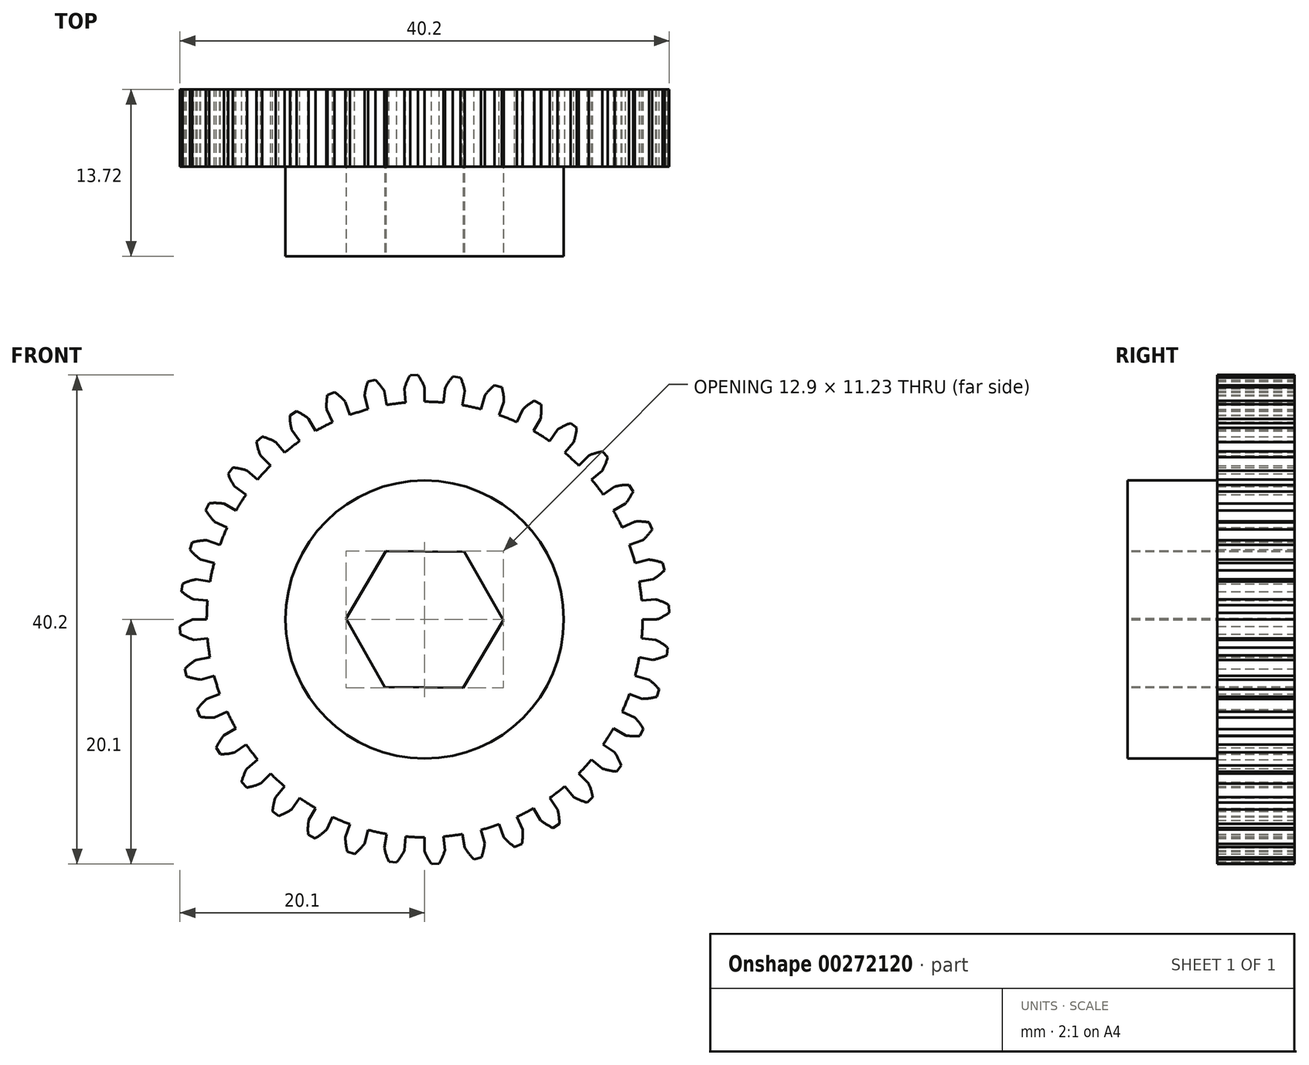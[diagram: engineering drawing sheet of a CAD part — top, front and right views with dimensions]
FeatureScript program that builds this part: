
annotation { "Feature Type Name" : "Feature", "Feature Type Description" : "" }
export const myFeature = defineFeature(function(context is Context, id is Id, definition is map)
    precondition{}
    {
        {
            var Q0;
            Q0=qCreatedBy(makeId("Front.planeOp"),FACE);
            var sketch = newSketch(context, id + "F0", { "sketchPlane" : qUnion([Q0])});
            skArc(sketch, "E0", {"start": v(-4.45, 17.34) * mm, "mid": v(-5.38, 17.07) * mm, "end": v(-6.3, 16.75) * mm});
            skLineSegment(sketch, "E1.trimOffspring", {"start": v(0, 23.81) * mm, "end": v(0, 30.83) * mm});
            skArc(sketch, "E2.trimOffspring", {"start": v(0, 19.05) * mm, "mid": v(-0.25, 19.6) * mm, "end": v(-0.56, 20.1) * mm});
            skArc(sketch, "E3.MirrorCS", {"start": v(-1.66, 18.98) * mm, "mid": v(-1.46, 19.54) * mm, "end": v(-1.2, 20.07) * mm});
            skLineSegment(sketch, "E4.trimOffspring", {"start": v(-1.56, 17.83) * mm, "end": v(-1.66, 18.98) * mm});
            skLineSegment(sketch, "E5.trimOffspring", {"start": v(0, 17.9) * mm, "end": v(0, 19.05) * mm});
            skArc(sketch, "E6.trimOffspring", {"start": v(0, 17.9) * mm, "mid": v(-0.1, 17.9) * mm, "end": v(-0.2, 17.9) * mm});
            skArc(sketch, "E7", {"start": v(-1.56, 17.84) * mm, "mid": v(-2.34, 17.75) * mm, "end": v(-3.1, 17.63) * mm});
            skLineSegment(sketch, "E8", {"start": v(-1.2, 20.07) * mm, "end": v(-0.56, 20.1) * mm});
            skLineSegment(sketch, "E9.1.0", {"start": v(-4.63, 17.3) * mm, "end": v(-4.93, 18.4) * mm});
            skArc(sketch, "E9.1.1", {"start": v(-4.93, 18.4) * mm, "mid": v(-4.83, 18.99) * mm, "end": v(-4.66, 19.56) * mm});
            skLineSegment(sketch, "E9.1.2", {"start": v(-4.66, 19.56) * mm, "end": v(-4.04, 19.7) * mm});
            skArc(sketch, "E9.1.3", {"start": v(-3.3, 18.76) * mm, "mid": v(-3.65, 19.25) * mm, "end": v(-4.04, 19.7) * mm});
            skLineSegment(sketch, "E9.1.4", {"start": v(-3.1, 17.63) * mm, "end": v(-3.3, 18.76) * mm});
            skLineSegment(sketch, "E9.2.0", {"start": v(-7.57, 16.22) * mm, "end": v(-8.05, 17.27) * mm});
            skArc(sketch, "E9.2.1", {"start": v(-8.05, 17.27) * mm, "mid": v(-8.05, 17.86) * mm, "end": v(-7.98, 18.45) * mm});
            skLineSegment(sketch, "E9.2.2", {"start": v(-7.98, 18.45) * mm, "end": v(-7.4, 18.7) * mm});
            skArc(sketch, "E9.2.3", {"start": v(-6.52, 17.9) * mm, "mid": v(-6.93, 18.32) * mm, "end": v(-7.4, 18.7) * mm});
            skLineSegment(sketch, "E9.2.4", {"start": v(-6.12, 16.82) * mm, "end": v(-6.52, 17.9) * mm});
            skLineSegment(sketch, "E9.3.0", {"start": v(-10.27, 14.66) * mm, "end": v(-10.93, 15.6) * mm});
            skArc(sketch, "E9.3.1", {"start": v(-10.93, 15.6) * mm, "mid": v(-11.03, 16.19) * mm, "end": v(-11.07, 16.78) * mm});
            skLineSegment(sketch, "E9.3.2", {"start": v(-11.07, 16.78) * mm, "end": v(-10.53, 17.12) * mm});
            skArc(sketch, "E9.3.3", {"start": v(-9.52, 16.5) * mm, "mid": v(-10, 16.84) * mm, "end": v(-10.53, 17.12) * mm});
            skLineSegment(sketch, "E9.3.4", {"start": v(-8.95, 15.5) * mm, "end": v(-9.53, 16.5) * mm});
            skLineSegment(sketch, "E9.4.0", {"start": v(-12.66, 12.66) * mm, "end": v(-13.47, 13.47) * mm});
            skArc(sketch, "E9.4.1", {"start": v(-13.47, 13.47) * mm, "mid": v(-13.68, 14.03) * mm, "end": v(-13.81, 14.6) * mm});
            skLineSegment(sketch, "E9.4.2", {"start": v(-13.81, 14.6) * mm, "end": v(-13.35, 15.03) * mm});
            skArc(sketch, "E9.4.3", {"start": v(-12.25, 14.6) * mm, "mid": v(-12.78, 14.85) * mm, "end": v(-13.35, 15.03) * mm});
            skLineSegment(sketch, "E9.4.4", {"start": v(-11.5, 13.71) * mm, "end": v(-12.25, 14.6) * mm});
            skLineSegment(sketch, "E9.5.0", {"start": v(-14.66, 10.27) * mm, "end": v(-15.6, 10.93) * mm});
            skArc(sketch, "E9.5.1", {"start": v(-15.6, 10.93) * mm, "mid": v(-15.9, 11.44) * mm, "end": v(-16.14, 11.99) * mm});
            skLineSegment(sketch, "E9.5.2", {"start": v(-16.14, 11.99) * mm, "end": v(-15.76, 12.49) * mm});
            skArc(sketch, "E9.5.3", {"start": v(-14.6, 12.25) * mm, "mid": v(-15.17, 12.4) * mm, "end": v(-15.76, 12.49) * mm});
            skLineSegment(sketch, "E9.5.4", {"start": v(-13.71, 11.5) * mm, "end": v(-14.6, 12.25) * mm});
            skLineSegment(sketch, "E9.6.0", {"start": v(-16.22, 7.57) * mm, "end": v(-17.27, 8.05) * mm});
            skArc(sketch, "E9.6.1", {"start": v(-17.27, 8.05) * mm, "mid": v(-17.65, 8.5) * mm, "end": v(-17.98, 9) * mm});
            skLineSegment(sketch, "E9.6.2", {"start": v(-17.98, 9) * mm, "end": v(-17.68, 9.56) * mm});
            skArc(sketch, "E9.6.3", {"start": v(-16.5, 9.53) * mm, "mid": v(-17.09, 9.58) * mm, "end": v(-17.68, 9.56) * mm});
            skLineSegment(sketch, "E9.6.4", {"start": v(-15.5, 8.95) * mm, "end": v(-16.5, 9.53) * mm});
            skLineSegment(sketch, "E9.7.0", {"start": v(-17.3, 4.63) * mm, "end": v(-18.4, 4.93) * mm});
            skArc(sketch, "E9.7.1", {"start": v(-18.4, 4.93) * mm, "mid": v(-18.86, 5.3) * mm, "end": v(-19.27, 5.74) * mm});
            skLineSegment(sketch, "E9.7.2", {"start": v(-19.27, 5.74) * mm, "end": v(-19.08, 6.35) * mm});
            skArc(sketch, "E9.7.3", {"start": v(-17.9, 6.52) * mm, "mid": v(-18.5, 6.47) * mm, "end": v(-19.08, 6.35) * mm});
            skLineSegment(sketch, "E9.7.4", {"start": v(-16.82, 6.12) * mm, "end": v(-17.9, 6.52) * mm});
            skLineSegment(sketch, "E9.8.0", {"start": v(-17.83, 1.56) * mm, "end": v(-18.98, 1.66) * mm});
            skArc(sketch, "E9.8.1", {"start": v(-18.98, 1.66) * mm, "mid": v(-19.5, 1.95) * mm, "end": v(-19.97, 2.31) * mm});
            skLineSegment(sketch, "E9.8.2", {"start": v(-19.97, 2.31) * mm, "end": v(-19.89, 2.94) * mm});
            skArc(sketch, "E9.8.3", {"start": v(-18.76, 3.3) * mm, "mid": v(-19.34, 3.16) * mm, "end": v(-19.89, 2.94) * mm});
            skLineSegment(sketch, "E9.8.4", {"start": v(-17.63, 3.1) * mm, "end": v(-18.76, 3.3) * mm});
            skLineSegment(sketch, "E9.9.0", {"start": v(-17.83, -1.56) * mm, "end": v(-18.98, -1.66) * mm});
            skArc(sketch, "E9.9.1", {"start": v(-18.98, -1.66) * mm, "mid": v(-19.54, -1.46) * mm, "end": v(-20.07, -1.2) * mm});
            skLineSegment(sketch, "E9.9.2", {"start": v(-20.07, -1.2) * mm, "end": v(-20.1, -0.56) * mm});
            skArc(sketch, "E9.9.3", {"start": v(-19.05, 0) * mm, "mid": v(-19.6, -0.25) * mm, "end": v(-20.1, -0.56) * mm});
            skLineSegment(sketch, "E9.9.4", {"start": v(-17.9, 0) * mm, "end": v(-19.05, 0) * mm});
            skLineSegment(sketch, "E9.10.0", {"start": v(-17.3, -4.63) * mm, "end": v(-18.4, -4.93) * mm});
            skArc(sketch, "E9.10.1", {"start": v(-18.4, -4.93) * mm, "mid": v(-18.99, -4.83) * mm, "end": v(-19.56, -4.66) * mm});
            skLineSegment(sketch, "E9.10.2", {"start": v(-19.56, -4.66) * mm, "end": v(-19.7, -4.04) * mm});
            skArc(sketch, "E9.10.3", {"start": v(-18.76, -3.3) * mm, "mid": v(-19.25, -3.65) * mm, "end": v(-19.7, -4.04) * mm});
            skLineSegment(sketch, "E9.10.4", {"start": v(-17.63, -3.1) * mm, "end": v(-18.76, -3.3) * mm});
            skLineSegment(sketch, "E9.11.0", {"start": v(-16.22, -7.57) * mm, "end": v(-17.27, -8.05) * mm});
            skArc(sketch, "E9.11.1", {"start": v(-17.27, -8.05) * mm, "mid": v(-17.86, -8.05) * mm, "end": v(-18.45, -7.98) * mm});
            skLineSegment(sketch, "E9.11.2", {"start": v(-18.45, -7.98) * mm, "end": v(-18.7, -7.4) * mm});
            skArc(sketch, "E9.11.3", {"start": v(-17.9, -6.52) * mm, "mid": v(-18.32, -6.93) * mm, "end": v(-18.7, -7.4) * mm});
            skLineSegment(sketch, "E9.11.4", {"start": v(-16.82, -6.12) * mm, "end": v(-17.9, -6.52) * mm});
            skLineSegment(sketch, "E9.12.0", {"start": v(-14.66, -10.27) * mm, "end": v(-15.6, -10.93) * mm});
            skArc(sketch, "E9.12.1", {"start": v(-15.6, -10.93) * mm, "mid": v(-16.19, -11.03) * mm, "end": v(-16.78, -11.07) * mm});
            skLineSegment(sketch, "E9.12.2", {"start": v(-16.78, -11.07) * mm, "end": v(-17.12, -10.53) * mm});
            skArc(sketch, "E9.12.3", {"start": v(-16.5, -9.52) * mm, "mid": v(-16.84, -10) * mm, "end": v(-17.12, -10.53) * mm});
            skLineSegment(sketch, "E9.12.4", {"start": v(-15.5, -8.95) * mm, "end": v(-16.5, -9.52) * mm});
            skLineSegment(sketch, "E9.13.0", {"start": v(-12.66, -12.66) * mm, "end": v(-13.47, -13.47) * mm});
            skArc(sketch, "E9.13.1", {"start": v(-13.47, -13.47) * mm, "mid": v(-14.03, -13.68) * mm, "end": v(-14.6, -13.81) * mm});
            skLineSegment(sketch, "E9.13.2", {"start": v(-14.6, -13.81) * mm, "end": v(-15.03, -13.35) * mm});
            skArc(sketch, "E9.13.3", {"start": v(-14.6, -12.25) * mm, "mid": v(-14.85, -12.78) * mm, "end": v(-15.03, -13.35) * mm});
            skLineSegment(sketch, "E9.13.4", {"start": v(-13.71, -11.5) * mm, "end": v(-14.6, -12.25) * mm});
            skLineSegment(sketch, "E9.14.0", {"start": v(-10.27, -14.66) * mm, "end": v(-10.93, -15.6) * mm});
            skArc(sketch, "E9.14.1", {"start": v(-10.93, -15.6) * mm, "mid": v(-11.44, -15.9) * mm, "end": v(-11.99, -16.14) * mm});
            skLineSegment(sketch, "E9.14.2", {"start": v(-11.99, -16.14) * mm, "end": v(-12.49, -15.76) * mm});
            skArc(sketch, "E9.14.3", {"start": v(-12.25, -14.6) * mm, "mid": v(-12.4, -15.17) * mm, "end": v(-12.49, -15.76) * mm});
            skLineSegment(sketch, "E9.14.4", {"start": v(-11.5, -13.71) * mm, "end": v(-12.25, -14.6) * mm});
            skLineSegment(sketch, "E9.15.0", {"start": v(-7.57, -16.22) * mm, "end": v(-8.05, -17.27) * mm});
            skArc(sketch, "E9.15.1", {"start": v(-8.05, -17.27) * mm, "mid": v(-8.5, -17.65) * mm, "end": v(-9, -17.98) * mm});
            skLineSegment(sketch, "E9.15.2", {"start": v(-9, -17.98) * mm, "end": v(-9.56, -17.68) * mm});
            skArc(sketch, "E9.15.3", {"start": v(-9.53, -16.5) * mm, "mid": v(-9.58, -17.09) * mm, "end": v(-9.56, -17.68) * mm});
            skLineSegment(sketch, "E9.15.4", {"start": v(-8.95, -15.5) * mm, "end": v(-9.53, -16.5) * mm});
            skLineSegment(sketch, "E9.16.0", {"start": v(-4.63, -17.3) * mm, "end": v(-4.93, -18.4) * mm});
            skArc(sketch, "E9.16.1", {"start": v(-4.93, -18.4) * mm, "mid": v(-5.3, -18.86) * mm, "end": v(-5.74, -19.27) * mm});
            skLineSegment(sketch, "E9.16.2", {"start": v(-5.74, -19.27) * mm, "end": v(-6.35, -19.08) * mm});
            skArc(sketch, "E9.16.3", {"start": v(-6.52, -17.9) * mm, "mid": v(-6.47, -18.5) * mm, "end": v(-6.35, -19.08) * mm});
            skLineSegment(sketch, "E9.16.4", {"start": v(-6.12, -16.82) * mm, "end": v(-6.52, -17.9) * mm});
            skLineSegment(sketch, "E9.17.0", {"start": v(-1.56, -17.83) * mm, "end": v(-1.66, -18.98) * mm});
            skArc(sketch, "E9.17.1", {"start": v(-1.66, -18.98) * mm, "mid": v(-1.95, -19.5) * mm, "end": v(-2.31, -19.97) * mm});
            skLineSegment(sketch, "E9.17.2", {"start": v(-2.31, -19.97) * mm, "end": v(-2.94, -19.89) * mm});
            skArc(sketch, "E9.17.3", {"start": v(-3.3, -18.76) * mm, "mid": v(-3.16, -19.34) * mm, "end": v(-2.94, -19.89) * mm});
            skLineSegment(sketch, "E9.17.4", {"start": v(-3.1, -17.63) * mm, "end": v(-3.3, -18.76) * mm});
            skLineSegment(sketch, "E9.18.0", {"start": v(1.56, -17.83) * mm, "end": v(1.66, -18.98) * mm});
            skArc(sketch, "E9.18.1", {"start": v(1.66, -18.98) * mm, "mid": v(1.46, -19.54) * mm, "end": v(1.2, -20.07) * mm});
            skLineSegment(sketch, "E9.18.2", {"start": v(1.2, -20.07) * mm, "end": v(0.56, -20.1) * mm});
            skArc(sketch, "E9.18.3", {"start": v(0, -19.05) * mm, "mid": v(0.25, -19.6) * mm, "end": v(0.56, -20.1) * mm});
            skLineSegment(sketch, "E9.18.4", {"start": v(0, -17.9) * mm, "end": v(0, -19.05) * mm});
            skLineSegment(sketch, "E9.19.0", {"start": v(4.63, -17.3) * mm, "end": v(4.93, -18.4) * mm});
            skArc(sketch, "E9.19.1", {"start": v(4.93, -18.4) * mm, "mid": v(4.83, -18.99) * mm, "end": v(4.66, -19.56) * mm});
            skLineSegment(sketch, "E9.19.2", {"start": v(4.66, -19.56) * mm, "end": v(4.04, -19.7) * mm});
            skArc(sketch, "E9.19.3", {"start": v(3.3, -18.76) * mm, "mid": v(3.65, -19.25) * mm, "end": v(4.04, -19.7) * mm});
            skLineSegment(sketch, "E9.19.4", {"start": v(3.1, -17.63) * mm, "end": v(3.3, -18.76) * mm});
            skLineSegment(sketch, "E9.20.0", {"start": v(7.57, -16.22) * mm, "end": v(8.05, -17.27) * mm});
            skArc(sketch, "E9.20.1", {"start": v(8.05, -17.27) * mm, "mid": v(8.05, -17.86) * mm, "end": v(7.98, -18.45) * mm});
            skLineSegment(sketch, "E9.20.2", {"start": v(7.98, -18.45) * mm, "end": v(7.4, -18.7) * mm});
            skArc(sketch, "E9.20.3", {"start": v(6.52, -17.9) * mm, "mid": v(6.93, -18.32) * mm, "end": v(7.4, -18.7) * mm});
            skLineSegment(sketch, "E9.20.4", {"start": v(6.12, -16.82) * mm, "end": v(6.52, -17.9) * mm});
            skLineSegment(sketch, "E9.21.0", {"start": v(10.27, -14.66) * mm, "end": v(10.93, -15.6) * mm});
            skArc(sketch, "E9.21.1", {"start": v(10.93, -15.6) * mm, "mid": v(11.03, -16.19) * mm, "end": v(11.07, -16.78) * mm});
            skLineSegment(sketch, "E9.21.2", {"start": v(11.07, -16.78) * mm, "end": v(10.53, -17.12) * mm});
            skArc(sketch, "E9.21.3", {"start": v(9.52, -16.5) * mm, "mid": v(10, -16.84) * mm, "end": v(10.53, -17.12) * mm});
            skLineSegment(sketch, "E9.21.4", {"start": v(8.95, -15.5) * mm, "end": v(9.53, -16.5) * mm});
            skLineSegment(sketch, "E9.22.0", {"start": v(12.66, -12.66) * mm, "end": v(13.47, -13.47) * mm});
            skArc(sketch, "E9.22.1", {"start": v(13.47, -13.47) * mm, "mid": v(13.68, -14.03) * mm, "end": v(13.81, -14.6) * mm});
            skLineSegment(sketch, "E9.22.2", {"start": v(13.81, -14.6) * mm, "end": v(13.35, -15.03) * mm});
            skArc(sketch, "E9.22.3", {"start": v(12.25, -14.6) * mm, "mid": v(12.78, -14.85) * mm, "end": v(13.35, -15.03) * mm});
            skLineSegment(sketch, "E9.22.4", {"start": v(11.5, -13.71) * mm, "end": v(12.25, -14.6) * mm});
            skLineSegment(sketch, "E9.23.0", {"start": v(14.66, -10.27) * mm, "end": v(15.6, -10.93) * mm});
            skArc(sketch, "E9.23.1", {"start": v(15.6, -10.93) * mm, "mid": v(15.9, -11.44) * mm, "end": v(16.14, -11.99) * mm});
            skLineSegment(sketch, "E9.23.2", {"start": v(16.14, -11.99) * mm, "end": v(15.76, -12.49) * mm});
            skArc(sketch, "E9.23.3", {"start": v(14.6, -12.25) * mm, "mid": v(15.17, -12.4) * mm, "end": v(15.76, -12.49) * mm});
            skLineSegment(sketch, "E9.23.4", {"start": v(13.71, -11.5) * mm, "end": v(14.6, -12.25) * mm});
            skLineSegment(sketch, "E9.24.0", {"start": v(16.22, -7.57) * mm, "end": v(17.27, -8.05) * mm});
            skArc(sketch, "E9.24.1", {"start": v(17.27, -8.05) * mm, "mid": v(17.65, -8.5) * mm, "end": v(17.98, -9) * mm});
            skLineSegment(sketch, "E9.24.2", {"start": v(17.98, -9) * mm, "end": v(17.68, -9.56) * mm});
            skArc(sketch, "E9.24.3", {"start": v(16.5, -9.53) * mm, "mid": v(17.09, -9.58) * mm, "end": v(17.68, -9.56) * mm});
            skLineSegment(sketch, "E9.24.4", {"start": v(15.5, -8.95) * mm, "end": v(16.5, -9.53) * mm});
            skLineSegment(sketch, "E9.25.0", {"start": v(17.3, -4.63) * mm, "end": v(18.4, -4.93) * mm});
            skArc(sketch, "E9.25.1", {"start": v(18.4, -4.93) * mm, "mid": v(18.86, -5.3) * mm, "end": v(19.27, -5.74) * mm});
            skLineSegment(sketch, "E9.25.2", {"start": v(19.27, -5.74) * mm, "end": v(19.08, -6.35) * mm});
            skArc(sketch, "E9.25.3", {"start": v(17.9, -6.52) * mm, "mid": v(18.5, -6.47) * mm, "end": v(19.08, -6.35) * mm});
            skLineSegment(sketch, "E9.25.4", {"start": v(16.82, -6.12) * mm, "end": v(17.9, -6.52) * mm});
            skLineSegment(sketch, "E9.26.0", {"start": v(17.83, -1.56) * mm, "end": v(18.98, -1.66) * mm});
            skArc(sketch, "E9.26.1", {"start": v(18.98, -1.66) * mm, "mid": v(19.5, -1.95) * mm, "end": v(19.97, -2.31) * mm});
            skLineSegment(sketch, "E9.26.2", {"start": v(19.97, -2.31) * mm, "end": v(19.89, -2.94) * mm});
            skArc(sketch, "E9.26.3", {"start": v(18.76, -3.3) * mm, "mid": v(19.34, -3.16) * mm, "end": v(19.89, -2.94) * mm});
            skLineSegment(sketch, "E9.26.4", {"start": v(17.63, -3.1) * mm, "end": v(18.76, -3.3) * mm});
            skLineSegment(sketch, "E9.27.0", {"start": v(17.83, 1.56) * mm, "end": v(18.98, 1.66) * mm});
            skArc(sketch, "E9.27.1", {"start": v(18.98, 1.66) * mm, "mid": v(19.54, 1.46) * mm, "end": v(20.07, 1.2) * mm});
            skLineSegment(sketch, "E9.27.2", {"start": v(20.07, 1.2) * mm, "end": v(20.1, 0.56) * mm});
            skArc(sketch, "E9.27.3", {"start": v(19.05, 0) * mm, "mid": v(19.6, 0.25) * mm, "end": v(20.1, 0.56) * mm});
            skLineSegment(sketch, "E9.27.4", {"start": v(17.9, 0) * mm, "end": v(19.05, 0) * mm});
            skLineSegment(sketch, "E9.28.0", {"start": v(17.3, 4.63) * mm, "end": v(18.4, 4.93) * mm});
            skArc(sketch, "E9.28.1", {"start": v(18.4, 4.93) * mm, "mid": v(18.99, 4.83) * mm, "end": v(19.56, 4.66) * mm});
            skLineSegment(sketch, "E9.28.2", {"start": v(19.56, 4.66) * mm, "end": v(19.7, 4.04) * mm});
            skArc(sketch, "E9.28.3", {"start": v(18.76, 3.3) * mm, "mid": v(19.25, 3.65) * mm, "end": v(19.7, 4.04) * mm});
            skLineSegment(sketch, "E9.28.4", {"start": v(17.63, 3.1) * mm, "end": v(18.76, 3.3) * mm});
            skLineSegment(sketch, "E9.29.0", {"start": v(16.22, 7.57) * mm, "end": v(17.27, 8.05) * mm});
            skArc(sketch, "E9.29.1", {"start": v(17.27, 8.05) * mm, "mid": v(17.86, 8.05) * mm, "end": v(18.45, 7.98) * mm});
            skLineSegment(sketch, "E9.29.2", {"start": v(18.45, 7.98) * mm, "end": v(18.7, 7.4) * mm});
            skArc(sketch, "E9.29.3", {"start": v(17.9, 6.52) * mm, "mid": v(18.32, 6.93) * mm, "end": v(18.7, 7.4) * mm});
            skLineSegment(sketch, "E9.29.4", {"start": v(16.82, 6.12) * mm, "end": v(17.9, 6.52) * mm});
            skLineSegment(sketch, "E9.30.0", {"start": v(14.66, 10.27) * mm, "end": v(15.6, 10.93) * mm});
            skArc(sketch, "E9.30.1", {"start": v(15.6, 10.93) * mm, "mid": v(16.19, 11.03) * mm, "end": v(16.78, 11.07) * mm});
            skLineSegment(sketch, "E9.30.2", {"start": v(16.78, 11.07) * mm, "end": v(17.12, 10.53) * mm});
            skArc(sketch, "E9.30.3", {"start": v(16.5, 9.52) * mm, "mid": v(16.84, 10) * mm, "end": v(17.12, 10.53) * mm});
            skLineSegment(sketch, "E9.30.4", {"start": v(15.5, 8.95) * mm, "end": v(16.5, 9.52) * mm});
            skLineSegment(sketch, "E9.31.0", {"start": v(12.66, 12.66) * mm, "end": v(13.47, 13.47) * mm});
            skArc(sketch, "E9.31.1", {"start": v(13.47, 13.47) * mm, "mid": v(14.03, 13.68) * mm, "end": v(14.6, 13.81) * mm});
            skLineSegment(sketch, "E9.31.2", {"start": v(14.6, 13.81) * mm, "end": v(15.03, 13.35) * mm});
            skArc(sketch, "E9.31.3", {"start": v(14.6, 12.25) * mm, "mid": v(14.85, 12.78) * mm, "end": v(15.03, 13.35) * mm});
            skLineSegment(sketch, "E9.31.4", {"start": v(13.71, 11.5) * mm, "end": v(14.6, 12.25) * mm});
            skLineSegment(sketch, "E9.32.0", {"start": v(10.27, 14.66) * mm, "end": v(10.93, 15.6) * mm});
            skArc(sketch, "E9.32.1", {"start": v(10.93, 15.6) * mm, "mid": v(11.44, 15.9) * mm, "end": v(11.99, 16.14) * mm});
            skLineSegment(sketch, "E9.32.2", {"start": v(11.99, 16.14) * mm, "end": v(12.49, 15.76) * mm});
            skArc(sketch, "E9.32.3", {"start": v(12.25, 14.6) * mm, "mid": v(12.4, 15.17) * mm, "end": v(12.49, 15.76) * mm});
            skLineSegment(sketch, "E9.32.4", {"start": v(11.5, 13.71) * mm, "end": v(12.25, 14.6) * mm});
            skLineSegment(sketch, "E9.33.0", {"start": v(7.57, 16.22) * mm, "end": v(8.05, 17.27) * mm});
            skArc(sketch, "E9.33.1", {"start": v(8.05, 17.27) * mm, "mid": v(8.5, 17.65) * mm, "end": v(9, 17.98) * mm});
            skLineSegment(sketch, "E9.33.2", {"start": v(9, 17.98) * mm, "end": v(9.56, 17.68) * mm});
            skArc(sketch, "E9.33.3", {"start": v(9.53, 16.5) * mm, "mid": v(9.58, 17.09) * mm, "end": v(9.56, 17.68) * mm});
            skLineSegment(sketch, "E9.33.4", {"start": v(8.95, 15.5) * mm, "end": v(9.52, 16.5) * mm});
            skLineSegment(sketch, "E9.34.0", {"start": v(4.63, 17.3) * mm, "end": v(4.93, 18.4) * mm});
            skArc(sketch, "E9.34.1", {"start": v(4.93, 18.4) * mm, "mid": v(5.3, 18.86) * mm, "end": v(5.74, 19.27) * mm});
            skLineSegment(sketch, "E9.34.2", {"start": v(5.74, 19.27) * mm, "end": v(6.35, 19.08) * mm});
            skArc(sketch, "E9.34.3", {"start": v(6.52, 17.9) * mm, "mid": v(6.47, 18.5) * mm, "end": v(6.35, 19.08) * mm});
            skLineSegment(sketch, "E9.34.4", {"start": v(6.12, 16.82) * mm, "end": v(6.52, 17.9) * mm});
            skLineSegment(sketch, "E9.35.0", {"start": v(1.56, 17.83) * mm, "end": v(1.66, 18.98) * mm});
            skArc(sketch, "E9.35.1", {"start": v(1.66, 18.98) * mm, "mid": v(1.95, 19.5) * mm, "end": v(2.31, 19.97) * mm});
            skLineSegment(sketch, "E9.35.2", {"start": v(2.31, 19.97) * mm, "end": v(2.94, 19.89) * mm});
            skArc(sketch, "E9.35.3", {"start": v(3.3, 18.76) * mm, "mid": v(3.16, 19.34) * mm, "end": v(2.94, 19.89) * mm});
            skLineSegment(sketch, "E9.35.4", {"start": v(3.1, 17.63) * mm, "end": v(3.3, 18.76) * mm});
            skArc(sketch, "E10.trimOffspring", {"start": v(-1.37, 17.85) * mm, "mid": v(-1.46, 17.84) * mm, "end": v(-1.56, 17.83) * mm});
            skArc(sketch, "E11.trimOffspring", {"start": v(1.56, 17.84) * mm, "mid": v(0.78, 17.89) * mm, "end": v(0, 17.9) * mm});
            skArc(sketch, "E12.trimOffspring", {"start": v(4.63, 17.3) * mm, "mid": v(3.88, 17.48) * mm, "end": v(3.1, 17.63) * mm});
            skArc(sketch, "E13.trimOffspring", {"start": v(4.82, 17.24) * mm, "mid": v(3.87, 17.48) * mm, "end": v(2.92, 17.66) * mm});
            skArc(sketch, "E14.trimOffspring", {"start": v(7.57, 16.23) * mm, "mid": v(6.85, 16.54) * mm, "end": v(6.12, 16.82) * mm});
            skArc(sketch, "E15.trimOffspring", {"start": v(7.74, 16.14) * mm, "mid": v(6.85, 16.54) * mm, "end": v(5.94, 16.89) * mm});
            skArc(sketch, "E16.trimOffspring", {"start": v(10.27, 14.67) * mm, "mid": v(9.62, 15.1) * mm, "end": v(8.95, 15.5) * mm});
            skArc(sketch, "E17.trimOffspring", {"start": v(10.43, 14.55) * mm, "mid": v(9.62, 15.1) * mm, "end": v(8.78, 15.6) * mm});
            skArc(sketch, "E18.trimOffspring", {"start": v(12.8, 12.52) * mm, "mid": v(12.1, 13.2) * mm, "end": v(11.36, 13.84) * mm});
            skArc(sketch, "E19.trimOffspring", {"start": v(14.67, 10.27) * mm, "mid": v(14.2, 10.9) * mm, "end": v(13.72, 11.5) * mm});
            skArc(sketch, "E20.trimOffspring", {"start": v(14.77, 10.1) * mm, "mid": v(14.2, 10.9) * mm, "end": v(13.59, 11.65) * mm});
            skArc(sketch, "E21.trimOffspring", {"start": v(16.23, 7.57) * mm, "mid": v(15.88, 8.27) * mm, "end": v(15.5, 8.95) * mm});
            skArc(sketch, "E22.trimOffspring", {"start": v(16.3, 7.39) * mm, "mid": v(15.88, 8.27) * mm, "end": v(15.4, 9.12) * mm});
            skArc(sketch, "E23.trimOffspring", {"start": v(17.34, 4.45) * mm, "mid": v(17.07, 5.38) * mm, "end": v(16.75, 6.3) * mm});
            skArc(sketch, "E24.trimOffspring", {"start": v(17.84, 1.56) * mm, "mid": v(17.75, 2.34) * mm, "end": v(17.63, 3.1) * mm});
            skArc(sketch, "E25.trimOffspring", {"start": v(17.85, 1.37) * mm, "mid": v(17.75, 2.34) * mm, "end": v(17.6, 3.3) * mm});
            skArc(sketch, "E26.trimOffspring", {"start": v(17.84, -1.56) * mm, "mid": v(17.89, -0.78) * mm, "end": v(17.9, 0) * mm});
            skArc(sketch, "E27.trimOffspring", {"start": v(17.82, -1.75) * mm, "mid": v(17.88, -0.78) * mm, "end": v(17.9, 0.2) * mm});
            skArc(sketch, "E28.trimOffspring", {"start": v(17.24, -4.82) * mm, "mid": v(17.48, -3.87) * mm, "end": v(17.66, -2.92) * mm});
            skArc(sketch, "E29.trimOffspring", {"start": v(16.23, -7.57) * mm, "mid": v(16.54, -6.85) * mm, "end": v(16.82, -6.12) * mm});
            skArc(sketch, "E30.trimOffspring", {"start": v(16.14, -7.74) * mm, "mid": v(16.54, -6.85) * mm, "end": v(16.89, -5.94) * mm});
            skArc(sketch, "E31.trimOffspring", {"start": v(14.55, -10.43) * mm, "mid": v(15.1, -9.62) * mm, "end": v(15.6, -8.78) * mm});
            skArc(sketch, "E32.trimOffspring", {"start": v(12.66, -12.66) * mm, "mid": v(13.2, -12.1) * mm, "end": v(13.72, -11.5) * mm});
            skArc(sketch, "E33.trimOffspring", {"start": v(12.52, -12.8) * mm, "mid": v(13.2, -12.1) * mm, "end": v(13.84, -11.36) * mm});
            skArc(sketch, "E34.trimOffspring", {"start": v(10.27, -14.67) * mm, "mid": v(10.9, -14.2) * mm, "end": v(11.5, -13.72) * mm});
            skArc(sketch, "E35.trimOffspring", {"start": v(10.1, -14.77) * mm, "mid": v(10.9, -14.2) * mm, "end": v(11.65, -13.59) * mm});
            skArc(sketch, "E36.trimOffspring", {"start": v(7.57, -16.23) * mm, "mid": v(8.27, -15.88) * mm, "end": v(8.95, -15.5) * mm});
            skArc(sketch, "E37.trimOffspring", {"start": v(7.39, -16.3) * mm, "mid": v(8.27, -15.88) * mm, "end": v(9.12, -15.4) * mm});
            skArc(sketch, "E38.trimOffspring", {"start": v(4.63, -17.3) * mm, "mid": v(5.38, -17.08) * mm, "end": v(6.12, -16.82) * mm});
            skArc(sketch, "E39.trimOffspring", {"start": v(4.45, -17.34) * mm, "mid": v(5.38, -17.07) * mm, "end": v(6.3, -16.75) * mm});
            skArc(sketch, "E40.trimOffspring", {"start": v(1.56, -17.84) * mm, "mid": v(2.34, -17.75) * mm, "end": v(3.1, -17.63) * mm});
            skArc(sketch, "E41.trimOffspring", {"start": v(1.37, -17.85) * mm, "mid": v(2.34, -17.75) * mm, "end": v(3.3, -17.6) * mm});
            skArc(sketch, "E42.trimOffspring", {"start": v(-1.56, -17.84) * mm, "mid": v(-0.78, -17.89) * mm, "end": v(0, -17.9) * mm});
            skArc(sketch, "E43.trimOffspring", {"start": v(-1.75, -17.82) * mm, "mid": v(-0.78, -17.88) * mm, "end": v(0.2, -17.9) * mm});
            skArc(sketch, "E44.trimOffspring", {"start": v(-4.63, -17.3) * mm, "mid": v(-3.88, -17.48) * mm, "end": v(-3.1, -17.63) * mm});
            skArc(sketch, "E45.trimOffspring", {"start": v(-4.82, -17.24) * mm, "mid": v(-3.87, -17.48) * mm, "end": v(-2.92, -17.66) * mm});
            skArc(sketch, "E46.trimOffspring", {"start": v(-7.57, -16.23) * mm, "mid": v(-6.85, -16.54) * mm, "end": v(-6.12, -16.82) * mm});
            skArc(sketch, "E47.trimOffspring", {"start": v(-7.74, -16.14) * mm, "mid": v(-6.94, -16.5) * mm, "end": v(-6.12, -16.82) * mm});
            skArc(sketch, "E48.trimOffspring", {"start": v(-10.43, -14.55) * mm, "mid": v(-9.62, -15.1) * mm, "end": v(-8.78, -15.6) * mm});
            skArc(sketch, "E49.trimOffspring", {"start": v(-12.66, -12.66) * mm, "mid": v(-12.1, -13.2) * mm, "end": v(-11.5, -13.72) * mm});
            skArc(sketch, "E50.trimOffspring", {"start": v(-12.8, -12.52) * mm, "mid": v(-12.1, -13.2) * mm, "end": v(-11.36, -13.84) * mm});
            skArc(sketch, "E51.trimOffspring", {"start": v(-14.67, -10.27) * mm, "mid": v(-14.2, -10.9) * mm, "end": v(-13.72, -11.5) * mm});
            skArc(sketch, "E52.trimOffspring", {"start": v(-14.77, -10.1) * mm, "mid": v(-14.2, -10.9) * mm, "end": v(-13.59, -11.65) * mm});
            skArc(sketch, "E53.trimOffspring", {"start": v(-16.23, -7.57) * mm, "mid": v(-15.88, -8.27) * mm, "end": v(-15.5, -8.95) * mm});
            skArc(sketch, "E54.trimOffspring", {"start": v(-16.3, -7.39) * mm, "mid": v(-15.88, -8.27) * mm, "end": v(-15.4, -9.12) * mm});
            skArc(sketch, "E55.trimOffspring", {"start": v(-17.3, -4.63) * mm, "mid": v(-17.08, -5.38) * mm, "end": v(-16.82, -6.12) * mm});
            skArc(sketch, "E56.trimOffspring", {"start": v(-17.34, -4.45) * mm, "mid": v(-17.07, -5.38) * mm, "end": v(-16.75, -6.3) * mm});
            skArc(sketch, "E57.trimOffspring", {"start": v(-17.84, -1.56) * mm, "mid": v(-17.75, -2.34) * mm, "end": v(-17.63, -3.1) * mm});
            skArc(sketch, "E58.trimOffspring", {"start": v(-17.85, -1.37) * mm, "mid": v(-17.75, -2.34) * mm, "end": v(-17.6, -3.3) * mm});
            skArc(sketch, "E59.trimOffspring", {"start": v(-17.84, 1.56) * mm, "mid": v(-17.89, 0.78) * mm, "end": v(-17.9, 0) * mm});
            skArc(sketch, "E60.trimOffspring", {"start": v(-17.82, 1.75) * mm, "mid": v(-17.88, 0.78) * mm, "end": v(-17.9, -0.2) * mm});
            skArc(sketch, "E61.trimOffspring", {"start": v(-17.3, 4.63) * mm, "mid": v(-17.48, 3.88) * mm, "end": v(-17.63, 3.1) * mm});
            skArc(sketch, "E62.trimOffspring", {"start": v(-17.24, 4.82) * mm, "mid": v(-17.48, 3.87) * mm, "end": v(-17.66, 2.92) * mm});
            skArc(sketch, "E63.trimOffspring", {"start": v(-16.23, 7.57) * mm, "mid": v(-16.54, 6.85) * mm, "end": v(-16.82, 6.12) * mm});
            skArc(sketch, "E64.trimOffspring", {"start": v(-16.14, 7.74) * mm, "mid": v(-16.54, 6.85) * mm, "end": v(-16.89, 5.94) * mm});
            skArc(sketch, "E65.trimOffspring", {"start": v(-14.55, 10.43) * mm, "mid": v(-15.1, 9.62) * mm, "end": v(-15.6, 8.78) * mm});
            skArc(sketch, "E66.trimOffspring", {"start": v(-12.66, 12.66) * mm, "mid": v(-13.2, 12.1) * mm, "end": v(-13.72, 11.5) * mm});
            skArc(sketch, "E67.trimOffspring", {"start": v(-12.52, 12.8) * mm, "mid": v(-13.2, 12.1) * mm, "end": v(-13.84, 11.36) * mm});
            skArc(sketch, "E68.trimOffspring", {"start": v(-10.27, 14.67) * mm, "mid": v(-10.9, 14.2) * mm, "end": v(-11.5, 13.72) * mm});
            skArc(sketch, "E69.trimOffspring", {"start": v(-10.1, 14.77) * mm, "mid": v(-10.9, 14.2) * mm, "end": v(-11.65, 13.59) * mm});
            skArc(sketch, "E70.trimOffspring", {"start": v(-7.57, 16.23) * mm, "mid": v(-8.27, 15.88) * mm, "end": v(-8.95, 15.5) * mm});
            skArc(sketch, "E71.trimOffspring", {"start": v(-7.39, 16.3) * mm, "mid": v(-8.27, 15.88) * mm, "end": v(-9.12, 15.4) * mm});
            skArc(sketch, "E72.trimOffspring", {"start": v(-4.63, 17.3) * mm, "mid": v(-5.38, 17.08) * mm, "end": v(-6.12, 16.82) * mm});
            skSolve(sketch);
        }
        {
            var Q0;
            {var subQ194=sQuery(id+"F0.wireOp",EDGE,"E2.trimOffspring");Q0=makeQuery(id+"F0.imprint","IMPRINT",FACE,{"disambiguationData":[TD([[makeQuery(id+"F0.imprint","IMPRINT",EDGE,{"derivedFrom":subQ194}),1.0]])]});}
            extrude(context, id + "F1", {"entities" : qUnion([Q0]), "depth" : 6.35 * mm});
        }
        {
            var Q0;
            Q0=makeQuery(id+"F1.opExtrude","CAP_FACE",FACE,{"disambiguationData":[OSD([sQuery(id+"F0.wireOp",EDGE,"E0"),sQuery(id+"F0.wireOp",EDGE,"E2.trimOffspring"),sQuery(id+"F0.wireOp",EDGE,"E3.MirrorCS"),sQuery(id+"F0.wireOp",EDGE,"E4.trimOffspring"),sQuery(id+"F0.wireOp",EDGE,"E5.trimOffspring"),sQuery(id+"F0.wireOp",EDGE,"E7"),sQuery(id+"F0.wireOp",EDGE,"E8"),sQuery(id+"F0.wireOp",EDGE,"E9.1.0"),sQuery(id+"F0.wireOp",EDGE,"E9.1.1"),sQuery(id+"F0.wireOp",EDGE,"E9.1.2"),sQuery(id+"F0.wireOp",EDGE,"E9.1.3"),sQuery(id+"F0.wireOp",EDGE,"E9.1.4"),sQuery(id+"F0.wireOp",EDGE,"E9.2.0"),sQuery(id+"F0.wireOp",EDGE,"E9.2.1"),sQuery(id+"F0.wireOp",EDGE,"E9.2.2"),sQuery(id+"F0.wireOp",EDGE,"E9.2.3"),sQuery(id+"F0.wireOp",EDGE,"E9.2.4"),sQuery(id+"F0.wireOp",EDGE,"E9.3.0"),sQuery(id+"F0.wireOp",EDGE,"E9.3.1"),sQuery(id+"F0.wireOp",EDGE,"E9.3.2"),sQuery(id+"F0.wireOp",EDGE,"E9.3.3"),sQuery(id+"F0.wireOp",EDGE,"E9.3.4"),sQuery(id+"F0.wireOp",EDGE,"E9.4.0"),sQuery(id+"F0.wireOp",EDGE,"E9.4.1"),sQuery(id+"F0.wireOp",EDGE,"E9.4.2"),sQuery(id+"F0.wireOp",EDGE,"E9.4.3"),sQuery(id+"F0.wireOp",EDGE,"E9.4.4"),sQuery(id+"F0.wireOp",EDGE,"E9.5.0"),sQuery(id+"F0.wireOp",EDGE,"E9.5.1"),sQuery(id+"F0.wireOp",EDGE,"E9.5.2"),sQuery(id+"F0.wireOp",EDGE,"E9.5.3"),sQuery(id+"F0.wireOp",EDGE,"E9.5.4"),sQuery(id+"F0.wireOp",EDGE,"E9.6.0"),sQuery(id+"F0.wireOp",EDGE,"E9.6.1"),sQuery(id+"F0.wireOp",EDGE,"E9.6.2"),sQuery(id+"F0.wireOp",EDGE,"E9.6.3"),sQuery(id+"F0.wireOp",EDGE,"E9.6.4"),sQuery(id+"F0.wireOp",EDGE,"E9.7.0"),sQuery(id+"F0.wireOp",EDGE,"E9.7.1"),sQuery(id+"F0.wireOp",EDGE,"E9.7.2"),sQuery(id+"F0.wireOp",EDGE,"E9.7.3"),sQuery(id+"F0.wireOp",EDGE,"E9.7.4"),sQuery(id+"F0.wireOp",EDGE,"E9.8.0"),sQuery(id+"F0.wireOp",EDGE,"E9.8.1"),sQuery(id+"F0.wireOp",EDGE,"E9.8.2"),sQuery(id+"F0.wireOp",EDGE,"E9.8.3"),sQuery(id+"F0.wireOp",EDGE,"E9.8.4"),sQuery(id+"F0.wireOp",EDGE,"E9.9.0"),sQuery(id+"F0.wireOp",EDGE,"E9.9.1"),sQuery(id+"F0.wireOp",EDGE,"E9.9.2"),sQuery(id+"F0.wireOp",EDGE,"E9.9.3"),sQuery(id+"F0.wireOp",EDGE,"E9.9.4"),sQuery(id+"F0.wireOp",EDGE,"E9.10.0"),sQuery(id+"F0.wireOp",EDGE,"E9.10.1"),sQuery(id+"F0.wireOp",EDGE,"E9.10.2"),sQuery(id+"F0.wireOp",EDGE,"E9.10.3"),sQuery(id+"F0.wireOp",EDGE,"E9.10.4"),sQuery(id+"F0.wireOp",EDGE,"E9.11.0"),sQuery(id+"F0.wireOp",EDGE,"E9.11.1"),sQuery(id+"F0.wireOp",EDGE,"E9.11.2"),sQuery(id+"F0.wireOp",EDGE,"E9.11.3"),sQuery(id+"F0.wireOp",EDGE,"E9.11.4"),sQuery(id+"F0.wireOp",EDGE,"E9.12.0"),sQuery(id+"F0.wireOp",EDGE,"E9.12.1"),sQuery(id+"F0.wireOp",EDGE,"E9.12.2"),sQuery(id+"F0.wireOp",EDGE,"E9.12.3"),sQuery(id+"F0.wireOp",EDGE,"E9.12.4"),sQuery(id+"F0.wireOp",EDGE,"E9.13.0"),sQuery(id+"F0.wireOp",EDGE,"E9.13.1"),sQuery(id+"F0.wireOp",EDGE,"E9.13.2"),sQuery(id+"F0.wireOp",EDGE,"E9.13.3"),sQuery(id+"F0.wireOp",EDGE,"E9.13.4"),sQuery(id+"F0.wireOp",EDGE,"E9.14.0"),sQuery(id+"F0.wireOp",EDGE,"E9.14.1"),sQuery(id+"F0.wireOp",EDGE,"E9.14.2"),sQuery(id+"F0.wireOp",EDGE,"E9.14.3"),sQuery(id+"F0.wireOp",EDGE,"E9.14.4"),sQuery(id+"F0.wireOp",EDGE,"E9.15.0"),sQuery(id+"F0.wireOp",EDGE,"E9.15.1"),sQuery(id+"F0.wireOp",EDGE,"E9.15.2"),sQuery(id+"F0.wireOp",EDGE,"E9.15.3"),sQuery(id+"F0.wireOp",EDGE,"E9.15.4"),sQuery(id+"F0.wireOp",EDGE,"E9.16.0"),sQuery(id+"F0.wireOp",EDGE,"E9.16.1"),sQuery(id+"F0.wireOp",EDGE,"E9.16.2"),sQuery(id+"F0.wireOp",EDGE,"E9.16.3"),sQuery(id+"F0.wireOp",EDGE,"E9.16.4"),sQuery(id+"F0.wireOp",EDGE,"E9.17.0"),sQuery(id+"F0.wireOp",EDGE,"E9.17.1"),sQuery(id+"F0.wireOp",EDGE,"E9.17.2"),sQuery(id+"F0.wireOp",EDGE,"E9.17.3"),sQuery(id+"F0.wireOp",EDGE,"E9.17.4"),sQuery(id+"F0.wireOp",EDGE,"E9.18.0"),sQuery(id+"F0.wireOp",EDGE,"E9.18.1"),sQuery(id+"F0.wireOp",EDGE,"E9.18.2"),sQuery(id+"F0.wireOp",EDGE,"E9.18.3"),sQuery(id+"F0.wireOp",EDGE,"E9.18.4"),sQuery(id+"F0.wireOp",EDGE,"E9.19.0"),sQuery(id+"F0.wireOp",EDGE,"E9.19.1"),sQuery(id+"F0.wireOp",EDGE,"E9.19.2"),sQuery(id+"F0.wireOp",EDGE,"E9.19.3"),sQuery(id+"F0.wireOp",EDGE,"E9.19.4"),sQuery(id+"F0.wireOp",EDGE,"E9.20.0"),sQuery(id+"F0.wireOp",EDGE,"E9.20.1"),sQuery(id+"F0.wireOp",EDGE,"E9.20.2"),sQuery(id+"F0.wireOp",EDGE,"E9.20.3"),sQuery(id+"F0.wireOp",EDGE,"E9.20.4"),sQuery(id+"F0.wireOp",EDGE,"E9.21.0"),sQuery(id+"F0.wireOp",EDGE,"E9.21.1"),sQuery(id+"F0.wireOp",EDGE,"E9.21.2"),sQuery(id+"F0.wireOp",EDGE,"E9.21.3"),sQuery(id+"F0.wireOp",EDGE,"E9.21.4"),sQuery(id+"F0.wireOp",EDGE,"E9.22.0"),sQuery(id+"F0.wireOp",EDGE,"E9.22.1"),sQuery(id+"F0.wireOp",EDGE,"E9.22.2"),sQuery(id+"F0.wireOp",EDGE,"E9.22.3"),sQuery(id+"F0.wireOp",EDGE,"E9.22.4"),sQuery(id+"F0.wireOp",EDGE,"E9.23.0"),sQuery(id+"F0.wireOp",EDGE,"E9.23.1"),sQuery(id+"F0.wireOp",EDGE,"E9.23.2"),sQuery(id+"F0.wireOp",EDGE,"E9.23.3"),sQuery(id+"F0.wireOp",EDGE,"E9.23.4"),sQuery(id+"F0.wireOp",EDGE,"E9.24.0"),sQuery(id+"F0.wireOp",EDGE,"E9.24.1"),sQuery(id+"F0.wireOp",EDGE,"E9.24.2"),sQuery(id+"F0.wireOp",EDGE,"E9.24.3"),sQuery(id+"F0.wireOp",EDGE,"E9.24.4"),sQuery(id+"F0.wireOp",EDGE,"E9.25.0"),sQuery(id+"F0.wireOp",EDGE,"E9.25.1"),sQuery(id+"F0.wireOp",EDGE,"E9.25.2"),sQuery(id+"F0.wireOp",EDGE,"E9.25.3"),sQuery(id+"F0.wireOp",EDGE,"E9.25.4"),sQuery(id+"F0.wireOp",EDGE,"E9.26.0"),sQuery(id+"F0.wireOp",EDGE,"E9.26.1"),sQuery(id+"F0.wireOp",EDGE,"E9.26.2"),sQuery(id+"F0.wireOp",EDGE,"E9.26.3"),sQuery(id+"F0.wireOp",EDGE,"E9.26.4"),sQuery(id+"F0.wireOp",EDGE,"E9.27.0"),sQuery(id+"F0.wireOp",EDGE,"E9.27.1"),sQuery(id+"F0.wireOp",EDGE,"E9.27.2"),sQuery(id+"F0.wireOp",EDGE,"E9.27.3"),sQuery(id+"F0.wireOp",EDGE,"E9.27.4"),sQuery(id+"F0.wireOp",EDGE,"E9.28.0"),sQuery(id+"F0.wireOp",EDGE,"E9.28.1"),sQuery(id+"F0.wireOp",EDGE,"E9.28.2"),sQuery(id+"F0.wireOp",EDGE,"E9.28.3"),sQuery(id+"F0.wireOp",EDGE,"E9.28.4"),sQuery(id+"F0.wireOp",EDGE,"E9.29.0"),sQuery(id+"F0.wireOp",EDGE,"E9.29.1"),sQuery(id+"F0.wireOp",EDGE,"E9.29.2"),sQuery(id+"F0.wireOp",EDGE,"E9.29.3"),sQuery(id+"F0.wireOp",EDGE,"E9.29.4"),sQuery(id+"F0.wireOp",EDGE,"E9.30.0"),sQuery(id+"F0.wireOp",EDGE,"E9.30.1"),sQuery(id+"F0.wireOp",EDGE,"E9.30.2"),sQuery(id+"F0.wireOp",EDGE,"E9.30.3"),sQuery(id+"F0.wireOp",EDGE,"E9.30.4"),sQuery(id+"F0.wireOp",EDGE,"E9.31.0"),sQuery(id+"F0.wireOp",EDGE,"E9.31.1"),sQuery(id+"F0.wireOp",EDGE,"E9.31.2"),sQuery(id+"F0.wireOp",EDGE,"E9.31.3"),sQuery(id+"F0.wireOp",EDGE,"E9.31.4"),sQuery(id+"F0.wireOp",EDGE,"E9.32.0"),sQuery(id+"F0.wireOp",EDGE,"E9.32.1"),sQuery(id+"F0.wireOp",EDGE,"E9.32.2"),sQuery(id+"F0.wireOp",EDGE,"E9.32.3"),sQuery(id+"F0.wireOp",EDGE,"E9.32.4"),sQuery(id+"F0.wireOp",EDGE,"E9.33.0"),sQuery(id+"F0.wireOp",EDGE,"E9.33.1"),sQuery(id+"F0.wireOp",EDGE,"E9.33.2"),sQuery(id+"F0.wireOp",EDGE,"E9.33.3"),sQuery(id+"F0.wireOp",EDGE,"E9.33.4"),sQuery(id+"F0.wireOp",EDGE,"E9.34.0"),sQuery(id+"F0.wireOp",EDGE,"E9.34.1"),sQuery(id+"F0.wireOp",EDGE,"E9.34.2"),sQuery(id+"F0.wireOp",EDGE,"E9.34.3"),sQuery(id+"F0.wireOp",EDGE,"E9.34.4"),sQuery(id+"F0.wireOp",EDGE,"E9.35.0"),sQuery(id+"F0.wireOp",EDGE,"E9.35.1"),sQuery(id+"F0.wireOp",EDGE,"E9.35.2"),sQuery(id+"F0.wireOp",EDGE,"E9.35.3"),sQuery(id+"F0.wireOp",EDGE,"E9.35.4"),sQuery(id+"F0.wireOp",EDGE,"E11.trimOffspring"),sQuery(id+"F0.wireOp",EDGE,"E13.trimOffspring"),sQuery(id+"F0.wireOp",EDGE,"E15.trimOffspring"),sQuery(id+"F0.wireOp",EDGE,"E17.trimOffspring"),sQuery(id+"F0.wireOp",EDGE,"E18.trimOffspring"),sQuery(id+"F0.wireOp",EDGE,"E20.trimOffspring"),sQuery(id+"F0.wireOp",EDGE,"E22.trimOffspring"),sQuery(id+"F0.wireOp",EDGE,"E23.trimOffspring"),sQuery(id+"F0.wireOp",EDGE,"E25.trimOffspring"),sQuery(id+"F0.wireOp",EDGE,"E27.trimOffspring"),sQuery(id+"F0.wireOp",EDGE,"E28.trimOffspring"),sQuery(id+"F0.wireOp",EDGE,"E30.trimOffspring"),sQuery(id+"F0.wireOp",EDGE,"E31.trimOffspring"),sQuery(id+"F0.wireOp",EDGE,"E33.trimOffspring"),sQuery(id+"F0.wireOp",EDGE,"E35.trimOffspring"),sQuery(id+"F0.wireOp",EDGE,"E37.trimOffspring"),sQuery(id+"F0.wireOp",EDGE,"E39.trimOffspring"),sQuery(id+"F0.wireOp",EDGE,"E41.trimOffspring"),sQuery(id+"F0.wireOp",EDGE,"E43.trimOffspring"),sQuery(id+"F0.wireOp",EDGE,"E45.trimOffspring"),sQuery(id+"F0.wireOp",EDGE,"E47.trimOffspring"),sQuery(id+"F0.wireOp",EDGE,"E48.trimOffspring"),sQuery(id+"F0.wireOp",EDGE,"E50.trimOffspring"),sQuery(id+"F0.wireOp",EDGE,"E52.trimOffspring"),sQuery(id+"F0.wireOp",EDGE,"E54.trimOffspring"),sQuery(id+"F0.wireOp",EDGE,"E56.trimOffspring"),sQuery(id+"F0.wireOp",EDGE,"E58.trimOffspring"),sQuery(id+"F0.wireOp",EDGE,"E60.trimOffspring"),sQuery(id+"F0.wireOp",EDGE,"E62.trimOffspring"),sQuery(id+"F0.wireOp",EDGE,"E64.trimOffspring"),sQuery(id+"F0.wireOp",EDGE,"E65.trimOffspring"),sQuery(id+"F0.wireOp",EDGE,"E67.trimOffspring"),sQuery(id+"F0.wireOp",EDGE,"E69.trimOffspring"),sQuery(id+"F0.wireOp",EDGE,"E71.trimOffspring")])],"isStart":false});
            var sketch = newSketch(context, id + "F2", { "sketchPlane" : qUnion([Q0])});
            skCircle(sketch, "E73", {"center": v(0, 0) * mm, "radius": 11.43 * mm});
            skSolve(sketch);
        }
        {
            var Q0;
            Q0=makeQuery(id+"F2.imprint","IMPRINT",FACE,{"disambiguationData":[TD([[makeQuery(id+"F2.imprint","IMPRINT",EDGE,{"derivedFrom":sQuery(id+"F2.wireOp",EDGE,"E73")}),1.0]])]});
            extrude(context, id + "F3", {"entities" : qUnion([Q0]), "operationType" : NewBodyOperationType.ADD, "depth" : 7.37 * mm});
        }
        {
            var Q0;
            Q0=makeQuery(id+"F3.opExtrude","CAP_FACE",FACE,{"disambiguationData":[OSD([sQuery(id+"F2.wireOp",EDGE,"E73")])],"isStart":false});
            var sketch = newSketch(context, id + "F4", { "sketchPlane" : qUnion([Q0])});
            skCircle(sketch, "E74.cCircle", {"center": v(0, 0) * mm, "radius": 5.59 * mm, "construction": true});
            skLineSegment(sketch, "E74.0", {"start": v(6.45, -0.06) * mm, "end": v(3.18, -5.62) * mm});
            skLineSegment(sketch, "E74.1", {"start": v(3.18, -5.62) * mm, "end": v(-3.28, -5.56) * mm});
            skLineSegment(sketch, "E74.2", {"start": v(-3.28, -5.56) * mm, "end": v(-6.45, 0.06) * mm});
            skLineSegment(sketch, "E74.3", {"start": v(-6.45, 0.06) * mm, "end": v(-3.18, 5.62) * mm});
            skLineSegment(sketch, "E74.4", {"start": v(-3.18, 5.62) * mm, "end": v(3.28, 5.56) * mm});
            skLineSegment(sketch, "E74.5", {"start": v(3.28, 5.56) * mm, "end": v(6.45, -0.06) * mm});
            skPoint(sketch, "E74.0.midPoint", {"position": v(4.81, -2.84) * mm});
            skSolve(sketch);
        }
        {
            var Q0;
            Q0=qSketchRegion(id+"F4",true);
            extrude(context, id + "F5", {"entities" : qUnion([Q0]), "operationType" : NewBodyOperationType.REMOVE, "oppositeDirection" : true, "depth" : 25.4 * mm});
        }
    });
